# Revit family: Zumtobel TECTON MIREL LED
name_source: partatom
category: Lighting Fixtures
revit_build: Autodesk Revit 2016 (Build: 20150220_1215(x64)
units: mm (PartAtom-declared; Revit-internal decimal feet)

## family parameters
Always vertical = Yes
Cut with Voids When Loaded = No
Light Source = Yes
OmniClass Number = 23.80.70.11
OmniClass Title = Luminaries for Internal Lighting
Part Type = Normal
Room Calculation Point = No
Round Connector Dimension = Use Diameter
Shared = Yes
Work Plane-Based = No

## types (3) — shared parameters
Color Filter = 16777215
Description = LED continuous row luminaire
Dimming Lamp Color Temperature Shift = <None>
Emit Shape Visible in Rendering = No
Emit from Rectangle Length = 54 mm  [stored 0.177165 ft]
Lamp = LED
Manufacturer = Zumtobel Ligthing
Tilt Angle = 90.00°
URL = http://www.zumtobel.com
Voltage = 230
Wattage Comments = 230
Width = 60 mm  [stored 0.19685 ft]

## per-type parameters (varying)
| type | Apparent Load | Emit from Rectangle Width | L 1000 | L 1500 | L 2000 | Length | Model | Photometric Web File |
| TECTON MIREL LED5400 L2000 | 38 VA | 2000 mm  [stored 6.56168 ft] | No | No | Yes | 2000 mm  [stored 6.56168 ft] | 42185316 | D38477AA_TECTON_MIREL_LED5400-840_L2000_LDE_WH.IES |
| TECTON MIREL LED4000 L1500 | 29 VA | 1500 mm  [stored 4.92126 ft] | No | Yes | No | 1500 mm  [stored 4.92126 ft] | 42185315 | D38477AA_TECTON_MIREL_LED4000-840_L1500_LDE_WH.IES |
| TECTON MIREL LED2700 L1000 | 20 VA | 1000 mm  [stored 3.28084 ft] | Yes | No | No | 1000 mm  [stored 3.28084 ft] | 42185314 | D38477AA_TECTON_MIREL_LED2700-840_L1000_LDE_WH.IES |

note: [stored X ft] marks values corroborated as IEEE doubles in the binary element streams (Revit-internal decimal feet)

## geometry (parser evidence)
native form markers: Blend x8, Sweep x9
no freeform markers — native parametric forms only
